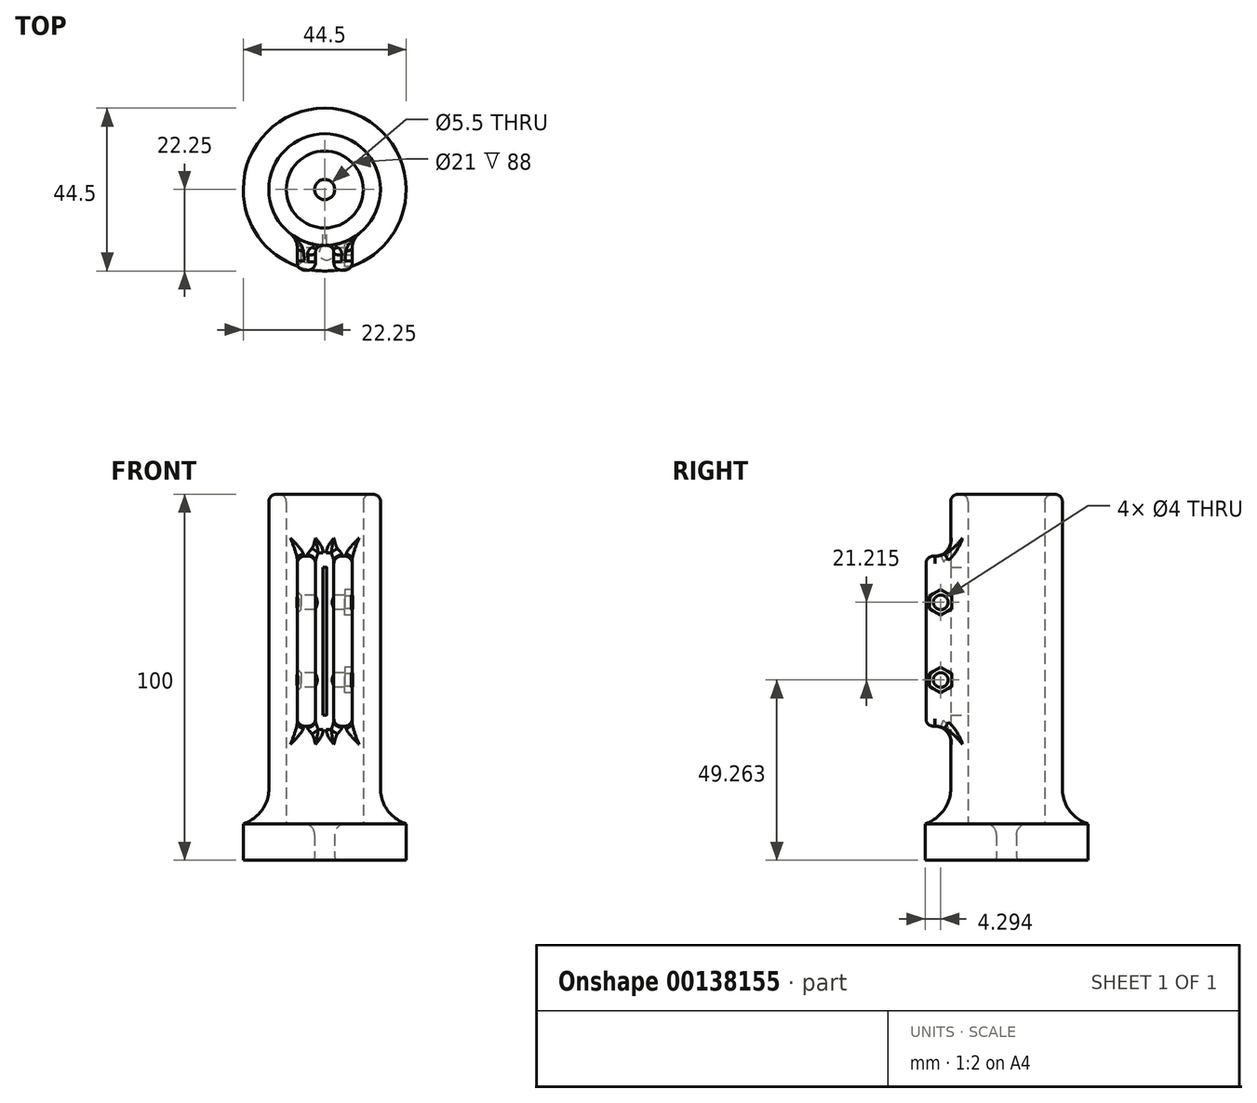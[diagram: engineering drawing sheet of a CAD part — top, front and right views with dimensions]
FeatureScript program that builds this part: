
annotation { "Feature Type Name" : "Feature", "Feature Type Description" : "" }
export const myFeature = defineFeature(function(context is Context, id is Id, definition is map)
    precondition{}
    {
        {
            var Q0;
            Q0=qCreatedBy(makeId("Top.planeOp"),FACE);
            var sketch = newSketch(context, id + "F0", { "sketchPlane" : qUnion([Q0])});
            skCircle(sketch, "E0", {"center": v(0, 0) * mm, "radius": 22.25 * mm});
            skCircle(sketch, "E1", {"center": v(0, 0) * mm, "radius": 2.75 * mm});
            skCircle(sketch, "E2", {"center": v(0, 0) * mm, "radius": 10.5 * mm});
            skCircle(sketch, "E3", {"center": v(0, 0) * mm, "radius": 15.25 * mm});
            skSolve(sketch);
        }
        {
            var Q0;
            Q0=makeQuery(id+"F0.imprint","IMPRINT",FACE,{"disambiguationData":[TD([[makeQuery(id+"F0.imprint","IMPRINT",EDGE,{"derivedFrom":sQuery(id+"F0.wireOp",EDGE,"E0")}),1.0]])]});
            var Q1;
            Q1=makeQuery(id+"F0.imprint","IMPRINT",FACE,{"disambiguationData":[TD([[makeQuery(id+"F0.imprint","IMPRINT",EDGE,{"derivedFrom":sQuery(id+"F0.wireOp",EDGE,"E2")}),-1.0]])]});
            var Q2;
            Q2=makeQuery(id+"F0.imprint","IMPRINT",FACE,{"disambiguationData":[TD([[makeQuery(id+"F0.imprint","IMPRINT",EDGE,{"derivedFrom":sQuery(id+"F0.wireOp",EDGE,"E1")}),-1.0]])]});
            extrude(context, id + "F1", {"entities" : qUnion([Q0, Q1, Q2]), "depth" : 10 * mm});
        }
        {
            var Q0;
            Q0=makeQuery(id+"F0.imprint","IMPRINT",FACE,{"disambiguationData":[TD([[makeQuery(id+"F0.imprint","IMPRINT",EDGE,{"derivedFrom":sQuery(id+"F0.wireOp",EDGE,"E2")}),-1.0]])]});
            extrude(context, id + "F2", {"entities" : qUnion([Q0]), "operationType" : NewBodyOperationType.ADD, "depth" : 100 * mm});
        }
        {
            var Q0;
            Q0=makeQuery(id+"F1.opExtrude","CAP_EDGE",EDGE,{"disambiguationData":[OSD([sQuery(id+"F0.wireOp",EDGE,"E1")])],"isStart":false});
            fillet(context, id + "F3", {"entities" : qUnion([Q0]), "radius" : 3 * mm, "tangentPropagation" : true, "allowEdgeOverflow" : false});
        }
        {
            var Q0;
            Q0=makeQuery(id+"F1.opExtrude","CAP_EDGE",EDGE,{"disambiguationData":[OSD([sQuery(id+"F0.wireOp",EDGE,"E1")])],"isStart":true});
            fillet(context, id + "F4", {"entities" : qUnion([Q0]), "radius" : 1 * mm, "tangentPropagation" : true, "allowEdgeOverflow" : false});
        }
        {
            var Q0;
            Q0=makeQuery(id+"F2.boolean.opBoolean","INTERSECT",EDGE,{"derivedFrom":[makeQuery(id+"F1.opExtrude","CAP_FACE",FACE,{"disambiguationData":[OSD([sQuery(id+"F0.wireOp",EDGE,"E0"),sQuery(id+"F0.wireOp",EDGE,"E1")])],"isStart":false}),makeQuery(id+"F2.opExtrude","SWEPT_FACE",FACE,{"disambiguationData":[OSD([sQuery(id+"F0.wireOp",EDGE,"E3")])]})]});
            fillet(context, id + "F5", {"entities" : qUnion([Q0]), "radius" : 10 * mm, "tangentPropagation" : true, "allowEdgeOverflow" : false});
        }
        {
            var Q0;
            Q0=makeQuery(id+"F2.opExtrude","CAP_EDGE",EDGE,{"disambiguationData":[OSD([sQuery(id+"F0.wireOp",EDGE,"E3")])],"isStart":false});
            fillet(context, id + "F6", {"entities" : qUnion([Q0]), "radius" : 2 * mm, "tangentPropagation" : true, "allowEdgeOverflow" : false});
        }
        {
            var Q0;
            Q0=makeQuery(id+"F2.opExtrude","CAP_EDGE",EDGE,{"disambiguationData":[OSD([sQuery(id+"F0.wireOp",EDGE,"E2")])],"isStart":false});
            fillet(context, id + "F7", {"entities" : qUnion([Q0]), "radius" : 2 * mm, "tangentPropagation" : true, "allowEdgeOverflow" : false});
        }
        {
            var Q0;
            Q0=qCreatedBy(makeId("Front.planeOp"),FACE);
            var sketch = newSketch(context, id + "F8", { "sketchPlane" : qUnion([Q0])});
            skPoint(sketch, "E4", {"position": v(0, 100.09) * mm});
            skPoint(sketch, "E5", {"position": v(0, 19.65) * mm});
            skPoint(sketch, "E6", {"position": v(0, 39.65) * mm});
            skPoint(sketch, "E7", {"position": v(0, 80.09) * mm});
            skPoint(sketch, "E8", {"position": v(0.5, 80.09) * mm});
            skPoint(sketch, "E9", {"position": v(-0.5, 80.09) * mm});
            skPoint(sketch, "E10", {"position": v(0.5, 39.65) * mm});
            skPoint(sketch, "E11", {"position": v(-0.5, 39.65) * mm});
            skLineSegment(sketch, "E12", {"start": v(-0.5, 80.09) * mm, "end": v(0.5, 80.09) * mm});
            skLineSegment(sketch, "E13", {"start": v(0.5, 39.65) * mm, "end": v(-0.5, 39.65) * mm});
            skLineSegment(sketch, "E14", {"start": v(-0.5, 39.65) * mm, "end": v(-0.5, 80.09) * mm});
            skLineSegment(sketch, "E15", {"start": v(0.5, 39.65) * mm, "end": v(0.5, 80.09) * mm});
            skPoint(sketch, "E16", {"position": v(-2.5, 83.09) * mm});
            skPoint(sketch, "E17", {"position": v(-2.5, 36.65) * mm});
            skPoint(sketch, "E18", {"position": v(-7.5, 83.09) * mm});
            skPoint(sketch, "E19", {"position": v(-7.5, 36.65) * mm});
            skLineSegment(sketch, "E20", {"start": v(-2.5, 36.65) * mm, "end": v(-7.5, 36.65) * mm});
            skLineSegment(sketch, "E21", {"start": v(-2.5, 83.09) * mm, "end": v(-2.5, 36.65) * mm});
            skLineSegment(sketch, "E22", {"start": v(-7.5, 83.09) * mm, "end": v(-7.5, 36.65) * mm});
            skLineSegment(sketch, "E23", {"start": v(-7.5, 83.09) * mm, "end": v(-2.5, 83.09) * mm});
            skPoint(sketch, "E24", {"position": v(-2.5, 80.09) * mm});
            skPoint(sketch, "E25", {"position": v(-2.5, 39.65) * mm});
            skPoint(sketch, "E26", {"position": v(2.5, 80.09) * mm});
            skPoint(sketch, "E27", {"position": v(2.5, 39.65) * mm});
            skPoint(sketch, "E28", {"position": v(2.5, 83.09) * mm});
            skPoint(sketch, "E29", {"position": v(2.5, 36.65) * mm});
            skLineSegment(sketch, "E30", {"start": v(2.5, 83.09) * mm, "end": v(2.5, 39.65) * mm});
            skLineSegment(sketch, "E31", {"start": v(2.5, 83.09) * mm, "end": v(7.5, 83.09) * mm});
            skLineSegment(sketch, "E32", {"start": v(2.5, 83.09) * mm, "end": v(2.5, 36.65) * mm});
            skLineSegment(sketch, "E33", {"start": v(7.5, 36.65) * mm, "end": v(2.5, 36.65) * mm});
            skLineSegment(sketch, "E34", {"start": v(7.5, 83.09) * mm, "end": v(7.5, 36.65) * mm});
            skSolve(sketch);
        }
        {
            var Q0;
            Q0=makeQuery(id+"F8.imprint","IMPRINT",FACE,{"disambiguationData":[TD([[makeQuery(id+"F8.imprint","IMPRINT",EDGE,{"derivedFrom":sQuery(id+"F8.wireOp",EDGE,"E12")}),-1.0]])]});
            extrude(context, id + "F9", {"entities" : qUnion([Q0]), "operationType" : NewBodyOperationType.REMOVE, "depth" : 50 * mm});
        }
        {
            var Q0;
            Q0=makeQuery(id+"F8.imprint","IMPRINT",FACE,{"disambiguationData":[TD([[makeQuery(id+"F8.imprint","IMPRINT",EDGE,{"derivedFrom":sQuery(id+"F8.wireOp",EDGE,"E20")}),-1.0]])]});
            var Q1;
            {var subQ0=sQuery(id+"F8.wireOp",EDGE,"E31");Q1=makeQuery(id+"F8.imprint","IMPRINT",FACE,{"disambiguationData":[TD([[makeQuery(id+"F8.imprint","IMPRINT",EDGE,{"derivedFrom":subQ0}),-1.0]])]});}
            extrude(context, id + "F10", {"entities" : qUnion([Q0, Q1]), "operationType" : NewBodyOperationType.ADD, "depth" : 22 * mm, "hasSecondDirection" : true, "secondDirectionOppositeDirection" : false, "secondDirectionDepth" : 10.1 * mm});
        }
        {
            var Q0;
            {var subQ0=sQuery(id+"F0.wireOp",EDGE,"E1");Q0=makeQuery(id+"F2.boolean.opBoolean","SPLIT",FACE,{"disambiguationData":[TD([makeQuery(id+"F1.opExtrude","SWEPT_FACE",FACE,{"disambiguationData":[OSD([subQ0])]})])],"derivedFrom":makeQuery(id+"F1.opExtrude","CAP_FACE",FACE,{"disambiguationData":[OSD([sQuery(id+"F0.wireOp",EDGE,"E0"),subQ0])],"isStart":false})});}
            var Q1;
            Q1=makeQuery(id+"F0.imprint","IMPRINT",FACE,{"disambiguationData":[TD([[makeQuery(id+"F0.imprint","IMPRINT",EDGE,{"derivedFrom":sQuery(id+"F0.wireOp",EDGE,"E1")}),1.0]])]});
            extrude(context, id + "F11", {"entities" : qUnion([Q0, Q1]), "operationType" : NewBodyOperationType.REMOVE, "depth" : 150 * mm});
        }
        {
            var Q0;
            Q0=makeQuery(id+"F10.boolean.opBoolean","INTERSECT",EDGE,{"derivedFrom":[makeQuery(id+"F2.opExtrude","SWEPT_FACE",FACE,{"disambiguationData":[OSD([sQuery(id+"F0.wireOp",EDGE,"E3")])]}),makeQuery(id+"F10.opExtrude","SWEPT_FACE",FACE,{"disambiguationData":[OSD([sQuery(id+"F8.wireOp",EDGE,"E23")])]})]});
            var Q1;
            Q1=makeQuery(id+"F10.boolean.opBoolean","INTERSECT",EDGE,{"derivedFrom":[makeQuery(id+"F2.opExtrude","SWEPT_FACE",FACE,{"disambiguationData":[OSD([sQuery(id+"F0.wireOp",EDGE,"E3")])]}),makeQuery(id+"F10.opExtrude","SWEPT_FACE",FACE,{"disambiguationData":[OSD([sQuery(id+"F8.wireOp",EDGE,"E31")])]})]});
            var Q2;
            Q2=makeQuery(id+"F10.boolean.opBoolean","INTERSECT",EDGE,{"derivedFrom":[makeQuery(id+"F2.opExtrude","SWEPT_FACE",FACE,{"disambiguationData":[OSD([sQuery(id+"F0.wireOp",EDGE,"E3")])]}),makeQuery(id+"F10.opExtrude","SWEPT_FACE",FACE,{"disambiguationData":[OSD([sQuery(id+"F8.wireOp",EDGE,"E33")])]})]});
            var Q3;
            Q3=makeQuery(id+"F10.boolean.opBoolean","INTERSECT",EDGE,{"derivedFrom":[makeQuery(id+"F2.opExtrude","SWEPT_FACE",FACE,{"disambiguationData":[OSD([sQuery(id+"F0.wireOp",EDGE,"E3")])]}),makeQuery(id+"F10.opExtrude","SWEPT_FACE",FACE,{"disambiguationData":[OSD([sQuery(id+"F8.wireOp",EDGE,"E20")])]})]});
            fillet(context, id + "F12", {"entities" : qUnion([Q0, Q1, Q2, Q3]), "radius" : 5 * mm, "tangentPropagation" : true, "allowEdgeOverflow" : false});
        }
        {
            var Q0;
            Q0=makeQuery(id+"F10.boolean.opBoolean","INTERSECT",EDGE,{"derivedFrom":[makeQuery(id+"F2.opExtrude","SWEPT_FACE",FACE,{"disambiguationData":[OSD([sQuery(id+"F0.wireOp",EDGE,"E3")])]}),makeQuery(id+"F10.opExtrude","SWEPT_FACE",FACE,{"disambiguationData":[OSD([sQuery(id+"F8.wireOp",EDGE,"E21")])]})]});
            var Q1;
            Q1=makeQuery(id+"F10.boolean.opBoolean","INTERSECT",EDGE,{"derivedFrom":[makeQuery(id+"F2.opExtrude","SWEPT_FACE",FACE,{"disambiguationData":[OSD([sQuery(id+"F0.wireOp",EDGE,"E3")])]}),makeQuery(id+"F10.opExtrude","SWEPT_FACE",FACE,{"disambiguationData":[OSD([sQuery(id+"F8.wireOp",EDGE,"E32")])]})]});
            fillet(context, id + "F13", {"entities" : qUnion([Q0, Q1]), "radius" : 2 * mm, "tangentPropagation" : true, "allowEdgeOverflow" : false});
        }
        {
            var Q0;
            Q0=makeQuery(id+"F10.boolean.opBoolean","INTERSECT",EDGE,{"derivedFrom":[makeQuery(id+"F2.opExtrude","SWEPT_FACE",FACE,{"disambiguationData":[OSD([sQuery(id+"F0.wireOp",EDGE,"E3")])]}),makeQuery(id+"F10.opExtrude","SWEPT_FACE",FACE,{"disambiguationData":[OSD([sQuery(id+"F8.wireOp",EDGE,"E22")])]})]});
            var Q1;
            Q1=makeQuery(id+"F10.boolean.opBoolean","INTERSECT",EDGE,{"derivedFrom":[makeQuery(id+"F2.opExtrude","SWEPT_FACE",FACE,{"disambiguationData":[OSD([sQuery(id+"F0.wireOp",EDGE,"E3")])]}),makeQuery(id+"F10.opExtrude","SWEPT_FACE",FACE,{"disambiguationData":[OSD([sQuery(id+"F8.wireOp",EDGE,"E34")])]})]});
            fillet(context, id + "F14", {"entities" : qUnion([Q0, Q1]), "radius" : 5 * mm, "tangentPropagation" : true, "allowEdgeOverflow" : false});
        }
        {
            var Q0;
            Q0=makeQuery(id+"F10.opExtrude","CAP_EDGE",EDGE,{"disambiguationData":[OSD([sQuery(id+"F8.wireOp",EDGE,"E31")])],"isStart":false});
            var Q1;
            Q1=makeQuery(id+"F10.opExtrude","CAP_EDGE",EDGE,{"disambiguationData":[OSD([sQuery(id+"F8.wireOp",EDGE,"E34")])],"isStart":false});
            var Q2;
            Q2=makeQuery(id+"F10.opExtrude","CAP_EDGE",EDGE,{"disambiguationData":[OSD([sQuery(id+"F8.wireOp",EDGE,"E33")])],"isStart":false});
            var Q3;
            Q3=makeQuery(id+"F10.opExtrude","CAP_EDGE",EDGE,{"disambiguationData":[OSD([sQuery(id+"F8.wireOp",EDGE,"E20")])],"isStart":false});
            var Q4;
            Q4=makeQuery(id+"F10.opExtrude","CAP_EDGE",EDGE,{"disambiguationData":[OSD([sQuery(id+"F8.wireOp",EDGE,"E22")])],"isStart":false});
            var Q5;
            Q5=makeQuery(id+"F10.opExtrude","CAP_EDGE",EDGE,{"disambiguationData":[OSD([sQuery(id+"F8.wireOp",EDGE,"E23")])],"isStart":false});
            fillet(context, id + "F15", {"entities" : qUnion([Q0, Q1, Q2, Q3, Q4, Q5]), "radius" : 2 * mm, "tangentPropagation" : true, "allowEdgeOverflow" : false});
        }
        {
            var Q0;
            {var subQ0=sQuery(id+"F0.wireOp",EDGE,"E3");Q0=makeQuery(id+"F14.opFillet","BLEND_EDGE",EDGE,{"blendedFrom":[makeQuery(id+"F10.boolean.opBoolean","INTERSECT",EDGE,{"derivedFrom":[makeQuery(id+"F2.opExtrude","SWEPT_FACE",FACE,{"disambiguationData":[OSD([subQ0])]}),makeQuery(id+"F10.opExtrude","SWEPT_FACE",FACE,{"disambiguationData":[OSD([sQuery(id+"F8.wireOp",EDGE,"E34")])]})]}),makeQuery(id+"F12.opFillet","BLEND_FACE",FACE,{"disambiguationData":[OSD([subQ0,sQuery(id+"F8.wireOp",EDGE,"E31")])]})],"blendedInto":[makeQuery(id+"F12.opFillet","BLEND_FACE",FACE,{"disambiguationData":[OSD([subQ0,sQuery(id+"F8.wireOp",EDGE,"E31")])]})]});}
            var Q1;
            {var subQ0=makeQuery(id+"F2.opExtrude","SWEPT_FACE",FACE,{"disambiguationData":[OSD([sQuery(id+"F0.wireOp",EDGE,"E3")])]});var subQ1=sQuery(id+"F8.wireOp",EDGE,"E31");var subQ2=makeQuery(id+"F10.opExtrude","SWEPT_FACE",FACE,{"disambiguationData":[OSD([subQ1])]});var subQ3=sQuery(id+"F8.wireOp",EDGE,"E34");Q1=makeQuery(id+"F12.opFillet","BLEND_EDGE",EDGE,{"blendedFrom":[makeQuery(id+"F10.boolean.opBoolean","INTERSECT",EDGE,{"derivedFrom":[subQ0,subQ2]}),makeQuery(id+"F10.boolean.opBoolean","SPLIT",FACE,{"disambiguationData":[TD([subQ0])],"derivedFrom":makeQuery(id+"F10.opExtrude","SWEPT_FACE",FACE,{"disambiguationData":[OSD([subQ3])]})})],"blendedInto":[makeQuery(id+"F10.boolean.opBoolean","SPLIT",FACE,{"disambiguationData":[TD([subQ0])],"derivedFrom":makeQuery(id+"F10.opExtrude","SWEPT_FACE",FACE,{"disambiguationData":[OSD([subQ3])]})})]});}
            var Q2;
            {var subQ0=makeQuery(id+"F2.opExtrude","SWEPT_FACE",FACE,{"disambiguationData":[OSD([sQuery(id+"F0.wireOp",EDGE,"E3")])]});var subQ1=sQuery(id+"F8.wireOp",EDGE,"E23");var subQ2=sQuery(id+"F8.wireOp",EDGE,"E22");var subQ4=makeQuery(id+"F10.opExtrude","SWEPT_FACE",FACE,{"disambiguationData":[OSD([subQ1])]});Q2=makeQuery(id+"F12.opFillet","BLEND_EDGE",EDGE,{"blendedFrom":[makeQuery(id+"F10.boolean.opBoolean","INTERSECT",EDGE,{"derivedFrom":[subQ0,subQ4]}),makeQuery(id+"F10.boolean.opBoolean","SPLIT",FACE,{"disambiguationData":[TD([subQ0])],"derivedFrom":makeQuery(id+"F10.opExtrude","SWEPT_FACE",FACE,{"disambiguationData":[OSD([subQ2])]})})],"blendedInto":[makeQuery(id+"F10.boolean.opBoolean","SPLIT",FACE,{"disambiguationData":[TD([subQ0])],"derivedFrom":makeQuery(id+"F10.opExtrude","SWEPT_FACE",FACE,{"disambiguationData":[OSD([subQ2])]})})]});}
            var Q3;
            {var subQ0=sQuery(id+"F0.wireOp",EDGE,"E3");Q3=makeQuery(id+"F14.opFillet","BLEND_EDGE",EDGE,{"blendedFrom":[makeQuery(id+"F10.boolean.opBoolean","INTERSECT",EDGE,{"derivedFrom":[makeQuery(id+"F2.opExtrude","SWEPT_FACE",FACE,{"disambiguationData":[OSD([subQ0])]}),makeQuery(id+"F10.opExtrude","SWEPT_FACE",FACE,{"disambiguationData":[OSD([sQuery(id+"F8.wireOp",EDGE,"E22")])]})]}),makeQuery(id+"F12.opFillet","BLEND_FACE",FACE,{"disambiguationData":[OSD([subQ0,sQuery(id+"F8.wireOp",EDGE,"E23")])]})],"blendedInto":[makeQuery(id+"F12.opFillet","BLEND_FACE",FACE,{"disambiguationData":[OSD([subQ0,sQuery(id+"F8.wireOp",EDGE,"E23")])]})]});}
            var Q4;
            {var subQ0=sQuery(id+"F0.wireOp",EDGE,"E3");Q4=makeQuery(id+"F13.opFillet","BLEND_EDGE",EDGE,{"blendedFrom":[makeQuery(id+"F10.boolean.opBoolean","INTERSECT",EDGE,{"derivedFrom":[makeQuery(id+"F2.opExtrude","SWEPT_FACE",FACE,{"disambiguationData":[OSD([subQ0])]}),makeQuery(id+"F10.opExtrude","SWEPT_FACE",FACE,{"disambiguationData":[OSD([sQuery(id+"F8.wireOp",EDGE,"E21")])]})]}),makeQuery(id+"F12.opFillet","BLEND_FACE",FACE,{"disambiguationData":[OSD([subQ0,sQuery(id+"F8.wireOp",EDGE,"E23")])]})],"blendedInto":[makeQuery(id+"F12.opFillet","BLEND_FACE",FACE,{"disambiguationData":[OSD([subQ0,sQuery(id+"F8.wireOp",EDGE,"E23")])]})]});}
            var Q5;
            {var subQ0=makeQuery(id+"F2.opExtrude","SWEPT_FACE",FACE,{"disambiguationData":[OSD([sQuery(id+"F0.wireOp",EDGE,"E3")])]});var subQ1=sQuery(id+"F8.wireOp",EDGE,"E23");var subQ2=sQuery(id+"F8.wireOp",EDGE,"E21");var subQ4=makeQuery(id+"F10.opExtrude","SWEPT_FACE",FACE,{"disambiguationData":[OSD([subQ1])]});Q5=makeQuery(id+"F12.opFillet","BLEND_EDGE",EDGE,{"blendedFrom":[makeQuery(id+"F10.boolean.opBoolean","INTERSECT",EDGE,{"derivedFrom":[subQ0,subQ4]}),makeQuery(id+"F10.boolean.opBoolean","SPLIT",FACE,{"disambiguationData":[TD([subQ0])],"derivedFrom":makeQuery(id+"F10.opExtrude","SWEPT_FACE",FACE,{"disambiguationData":[OSD([subQ2])]})})],"blendedInto":[makeQuery(id+"F10.boolean.opBoolean","SPLIT",FACE,{"disambiguationData":[TD([subQ0])],"derivedFrom":makeQuery(id+"F10.opExtrude","SWEPT_FACE",FACE,{"disambiguationData":[OSD([subQ2])]})})]});}
            var Q6;
            {var subQ0=sQuery(id+"F0.wireOp",EDGE,"E3");Q6=makeQuery(id+"F13.opFillet","BLEND_EDGE",EDGE,{"blendedFrom":[makeQuery(id+"F10.boolean.opBoolean","INTERSECT",EDGE,{"derivedFrom":[makeQuery(id+"F2.opExtrude","SWEPT_FACE",FACE,{"disambiguationData":[OSD([subQ0])]}),makeQuery(id+"F10.opExtrude","SWEPT_FACE",FACE,{"disambiguationData":[OSD([sQuery(id+"F8.wireOp",EDGE,"E32")])]})]}),makeQuery(id+"F12.opFillet","BLEND_FACE",FACE,{"disambiguationData":[OSD([subQ0,sQuery(id+"F8.wireOp",EDGE,"E31")])]})],"blendedInto":[makeQuery(id+"F12.opFillet","BLEND_FACE",FACE,{"disambiguationData":[OSD([subQ0,sQuery(id+"F8.wireOp",EDGE,"E31")])]})]});}
            var Q7;
            {var subQ0=makeQuery(id+"F2.opExtrude","SWEPT_FACE",FACE,{"disambiguationData":[OSD([sQuery(id+"F0.wireOp",EDGE,"E3")])]});var subQ1=sQuery(id+"F8.wireOp",EDGE,"E31");var subQ2=makeQuery(id+"F10.opExtrude","SWEPT_FACE",FACE,{"disambiguationData":[OSD([subQ1])]});var subQ4=sQuery(id+"F8.wireOp",EDGE,"E32");Q7=makeQuery(id+"F12.opFillet","BLEND_EDGE",EDGE,{"blendedFrom":[makeQuery(id+"F10.boolean.opBoolean","INTERSECT",EDGE,{"derivedFrom":[subQ0,subQ2]}),makeQuery(id+"F10.boolean.opBoolean","SPLIT",FACE,{"disambiguationData":[TD([subQ0])],"derivedFrom":makeQuery(id+"F10.opExtrude","SWEPT_FACE",FACE,{"disambiguationData":[OSD([subQ4])]})})],"blendedInto":[makeQuery(id+"F10.boolean.opBoolean","SPLIT",FACE,{"disambiguationData":[TD([subQ0])],"derivedFrom":makeQuery(id+"F10.opExtrude","SWEPT_FACE",FACE,{"disambiguationData":[OSD([subQ4])]})})]});}
            var Q8;
            {var subQ0=sQuery(id+"F8.wireOp",EDGE,"E31");var subQ1=sQuery(id+"F8.wireOp",EDGE,"E34");Q8=makeQuery(id+"F10.boolean.opBoolean","SPLIT",EDGE,{"disambiguationData":[TD([makeQuery(id+"F2.opExtrude","SWEPT_FACE",FACE,{"disambiguationData":[OSD([sQuery(id+"F0.wireOp",EDGE,"E3")])]})])],"derivedFrom":makeQuery(id+"F10.opExtrude","SWEPT_EDGE",EDGE,{"disambiguationData":[OSD([subQ0,subQ1])]})});}
            var Q9;
            Q9=makeQuery(id+"F15.opFillet","BLEND_EDGE",EDGE,{"blendedFrom":[makeQuery(id+"F10.opExtrude","CAP_EDGE",EDGE,{"disambiguationData":[OSD([sQuery(id+"F8.wireOp",EDGE,"E31")])],"isStart":false}),makeQuery(id+"F10.opExtrude","CAP_EDGE",EDGE,{"disambiguationData":[OSD([sQuery(id+"F8.wireOp",EDGE,"E34")])],"isStart":false})],"blendedInto":[]});
            var Q10;
            {var subQ0=sQuery(id+"F8.wireOp",EDGE,"E31");var subQ2=sQuery(id+"F8.wireOp",EDGE,"E32");Q10=makeQuery(id+"F15.opFillet","BLEND_EDGE",EDGE,{"blendedFrom":[makeQuery(id+"F10.opExtrude","CAP_EDGE",EDGE,{"disambiguationData":[OSD([subQ0])],"isStart":false}),makeQuery(id+"F10.boolean.opBoolean","SPLIT",FACE,{"disambiguationData":[TD([makeQuery(id+"F2.opExtrude","SWEPT_FACE",FACE,{"disambiguationData":[OSD([sQuery(id+"F0.wireOp",EDGE,"E3")])]})])],"derivedFrom":makeQuery(id+"F10.opExtrude","SWEPT_FACE",FACE,{"disambiguationData":[OSD([subQ2])]})})],"blendedInto":[makeQuery(id+"F10.boolean.opBoolean","SPLIT",FACE,{"disambiguationData":[TD([makeQuery(id+"F2.opExtrude","SWEPT_FACE",FACE,{"disambiguationData":[OSD([sQuery(id+"F0.wireOp",EDGE,"E3")])]})])],"derivedFrom":makeQuery(id+"F10.opExtrude","SWEPT_FACE",FACE,{"disambiguationData":[OSD([subQ2])]})})]});}
            var Q11;
            {var subQ0=sQuery(id+"F8.wireOp",EDGE,"E23");var subQ1=sQuery(id+"F8.wireOp",EDGE,"E21");Q11=makeQuery(id+"F15.opFillet","BLEND_EDGE",EDGE,{"blendedFrom":[makeQuery(id+"F10.opExtrude","CAP_EDGE",EDGE,{"disambiguationData":[OSD([subQ0])],"isStart":false}),makeQuery(id+"F10.boolean.opBoolean","SPLIT",FACE,{"disambiguationData":[TD([makeQuery(id+"F2.opExtrude","SWEPT_FACE",FACE,{"disambiguationData":[OSD([sQuery(id+"F0.wireOp",EDGE,"E3")])]})])],"derivedFrom":makeQuery(id+"F10.opExtrude","SWEPT_FACE",FACE,{"disambiguationData":[OSD([subQ1])]})})],"blendedInto":[makeQuery(id+"F10.boolean.opBoolean","SPLIT",FACE,{"disambiguationData":[TD([makeQuery(id+"F2.opExtrude","SWEPT_FACE",FACE,{"disambiguationData":[OSD([sQuery(id+"F0.wireOp",EDGE,"E3")])]})])],"derivedFrom":makeQuery(id+"F10.opExtrude","SWEPT_FACE",FACE,{"disambiguationData":[OSD([subQ1])]})})]});}
            var Q12;
            {var subQ0=sQuery(id+"F8.wireOp",EDGE,"E23");var subQ1=sQuery(id+"F8.wireOp",EDGE,"E22");Q12=makeQuery(id+"F10.boolean.opBoolean","SPLIT",EDGE,{"disambiguationData":[TD([makeQuery(id+"F2.opExtrude","SWEPT_FACE",FACE,{"disambiguationData":[OSD([sQuery(id+"F0.wireOp",EDGE,"E3")])]})])],"derivedFrom":makeQuery(id+"F10.opExtrude","SWEPT_EDGE",EDGE,{"disambiguationData":[OSD([subQ1,subQ0])]})});}
            var Q13;
            Q13=makeQuery(id+"F15.opFillet","BLEND_EDGE",EDGE,{"blendedFrom":[makeQuery(id+"F10.opExtrude","CAP_EDGE",EDGE,{"disambiguationData":[OSD([sQuery(id+"F8.wireOp",EDGE,"E22")])],"isStart":false}),makeQuery(id+"F10.opExtrude","CAP_EDGE",EDGE,{"disambiguationData":[OSD([sQuery(id+"F8.wireOp",EDGE,"E23")])],"isStart":false})],"blendedInto":[]});
            var Q14;
            {var subQ0=sQuery(id+"F0.wireOp",EDGE,"E3");Q14=makeQuery(id+"F14.opFillet","BLEND_EDGE",EDGE,{"blendedFrom":[makeQuery(id+"F10.boolean.opBoolean","INTERSECT",EDGE,{"derivedFrom":[makeQuery(id+"F2.opExtrude","SWEPT_FACE",FACE,{"disambiguationData":[OSD([subQ0])]}),makeQuery(id+"F10.opExtrude","SWEPT_FACE",FACE,{"disambiguationData":[OSD([sQuery(id+"F8.wireOp",EDGE,"E34")])]})]}),makeQuery(id+"F12.opFillet","BLEND_FACE",FACE,{"disambiguationData":[OSD([subQ0,sQuery(id+"F8.wireOp",EDGE,"E33")])]})],"blendedInto":[makeQuery(id+"F12.opFillet","BLEND_FACE",FACE,{"disambiguationData":[OSD([subQ0,sQuery(id+"F8.wireOp",EDGE,"E33")])]})]});}
            var Q15;
            {var subQ0=makeQuery(id+"F2.opExtrude","SWEPT_FACE",FACE,{"disambiguationData":[OSD([sQuery(id+"F0.wireOp",EDGE,"E3")])]});var subQ2=sQuery(id+"F8.wireOp",EDGE,"E34");var subQ3=sQuery(id+"F8.wireOp",EDGE,"E33");var subQ4=makeQuery(id+"F10.opExtrude","SWEPT_FACE",FACE,{"disambiguationData":[OSD([subQ3])]});Q15=makeQuery(id+"F12.opFillet","BLEND_EDGE",EDGE,{"blendedFrom":[makeQuery(id+"F10.boolean.opBoolean","INTERSECT",EDGE,{"derivedFrom":[subQ0,subQ4]}),makeQuery(id+"F10.boolean.opBoolean","SPLIT",FACE,{"disambiguationData":[TD([subQ0])],"derivedFrom":makeQuery(id+"F10.opExtrude","SWEPT_FACE",FACE,{"disambiguationData":[OSD([subQ2])]})})],"blendedInto":[makeQuery(id+"F10.boolean.opBoolean","SPLIT",FACE,{"disambiguationData":[TD([subQ0])],"derivedFrom":makeQuery(id+"F10.opExtrude","SWEPT_FACE",FACE,{"disambiguationData":[OSD([subQ2])]})})]});}
            var Q16;
            {var subQ0=sQuery(id+"F8.wireOp",EDGE,"E34");var subQ1=sQuery(id+"F8.wireOp",EDGE,"E33");Q16=makeQuery(id+"F10.boolean.opBoolean","SPLIT",EDGE,{"disambiguationData":[TD([makeQuery(id+"F2.opExtrude","SWEPT_FACE",FACE,{"disambiguationData":[OSD([sQuery(id+"F0.wireOp",EDGE,"E3")])]})])],"derivedFrom":makeQuery(id+"F10.opExtrude","SWEPT_EDGE",EDGE,{"disambiguationData":[OSD([subQ1,subQ0])]})});}
            var Q17;
            Q17=makeQuery(id+"F15.opFillet","BLEND_EDGE",EDGE,{"blendedFrom":[makeQuery(id+"F10.opExtrude","CAP_EDGE",EDGE,{"disambiguationData":[OSD([sQuery(id+"F8.wireOp",EDGE,"E33")])],"isStart":false}),makeQuery(id+"F10.opExtrude","CAP_EDGE",EDGE,{"disambiguationData":[OSD([sQuery(id+"F8.wireOp",EDGE,"E34")])],"isStart":false})],"blendedInto":[]});
            var Q18;
            {var subQ1=sQuery(id+"F8.wireOp",EDGE,"E33");var subQ2=sQuery(id+"F8.wireOp",EDGE,"E32");Q18=makeQuery(id+"F15.opFillet","BLEND_EDGE",EDGE,{"blendedFrom":[makeQuery(id+"F10.opExtrude","CAP_EDGE",EDGE,{"disambiguationData":[OSD([subQ1])],"isStart":false}),makeQuery(id+"F10.boolean.opBoolean","SPLIT",FACE,{"disambiguationData":[TD([makeQuery(id+"F2.opExtrude","SWEPT_FACE",FACE,{"disambiguationData":[OSD([sQuery(id+"F0.wireOp",EDGE,"E3")])]})])],"derivedFrom":makeQuery(id+"F10.opExtrude","SWEPT_FACE",FACE,{"disambiguationData":[OSD([subQ2])]})})],"blendedInto":[makeQuery(id+"F10.boolean.opBoolean","SPLIT",FACE,{"disambiguationData":[TD([makeQuery(id+"F2.opExtrude","SWEPT_FACE",FACE,{"disambiguationData":[OSD([sQuery(id+"F0.wireOp",EDGE,"E3")])]})])],"derivedFrom":makeQuery(id+"F10.opExtrude","SWEPT_FACE",FACE,{"disambiguationData":[OSD([subQ2])]})})]});}
            var Q19;
            {var subQ0=makeQuery(id+"F2.opExtrude","SWEPT_FACE",FACE,{"disambiguationData":[OSD([sQuery(id+"F0.wireOp",EDGE,"E3")])]});var subQ2=sQuery(id+"F8.wireOp",EDGE,"E33");var subQ3=sQuery(id+"F8.wireOp",EDGE,"E32");var subQ4=makeQuery(id+"F10.opExtrude","SWEPT_FACE",FACE,{"disambiguationData":[OSD([subQ2])]});Q19=makeQuery(id+"F12.opFillet","BLEND_EDGE",EDGE,{"blendedFrom":[makeQuery(id+"F10.boolean.opBoolean","INTERSECT",EDGE,{"derivedFrom":[subQ0,subQ4]}),makeQuery(id+"F10.boolean.opBoolean","SPLIT",FACE,{"disambiguationData":[TD([subQ0])],"derivedFrom":makeQuery(id+"F10.opExtrude","SWEPT_FACE",FACE,{"disambiguationData":[OSD([subQ3])]})})],"blendedInto":[makeQuery(id+"F10.boolean.opBoolean","SPLIT",FACE,{"disambiguationData":[TD([subQ0])],"derivedFrom":makeQuery(id+"F10.opExtrude","SWEPT_FACE",FACE,{"disambiguationData":[OSD([subQ3])]})})]});}
            var Q20;
            {var subQ0=sQuery(id+"F0.wireOp",EDGE,"E3");Q20=makeQuery(id+"F13.opFillet","BLEND_EDGE",EDGE,{"blendedFrom":[makeQuery(id+"F10.boolean.opBoolean","INTERSECT",EDGE,{"derivedFrom":[makeQuery(id+"F2.opExtrude","SWEPT_FACE",FACE,{"disambiguationData":[OSD([subQ0])]}),makeQuery(id+"F10.opExtrude","SWEPT_FACE",FACE,{"disambiguationData":[OSD([sQuery(id+"F8.wireOp",EDGE,"E32")])]})]}),makeQuery(id+"F12.opFillet","BLEND_FACE",FACE,{"disambiguationData":[OSD([subQ0,sQuery(id+"F8.wireOp",EDGE,"E33")])]})],"blendedInto":[makeQuery(id+"F12.opFillet","BLEND_FACE",FACE,{"disambiguationData":[OSD([subQ0,sQuery(id+"F8.wireOp",EDGE,"E33")])]})]});}
            var Q21;
            {var subQ0=sQuery(id+"F0.wireOp",EDGE,"E3");Q21=makeQuery(id+"F13.opFillet","BLEND_EDGE",EDGE,{"blendedFrom":[makeQuery(id+"F10.boolean.opBoolean","INTERSECT",EDGE,{"derivedFrom":[makeQuery(id+"F2.opExtrude","SWEPT_FACE",FACE,{"disambiguationData":[OSD([subQ0])]}),makeQuery(id+"F10.opExtrude","SWEPT_FACE",FACE,{"disambiguationData":[OSD([sQuery(id+"F8.wireOp",EDGE,"E21")])]})]}),makeQuery(id+"F12.opFillet","BLEND_FACE",FACE,{"disambiguationData":[OSD([subQ0,sQuery(id+"F8.wireOp",EDGE,"E20")])]})],"blendedInto":[makeQuery(id+"F12.opFillet","BLEND_FACE",FACE,{"disambiguationData":[OSD([subQ0,sQuery(id+"F8.wireOp",EDGE,"E20")])]})]});}
            var Q22;
            {var subQ0=makeQuery(id+"F2.opExtrude","SWEPT_FACE",FACE,{"disambiguationData":[OSD([sQuery(id+"F0.wireOp",EDGE,"E3")])]});var subQ2=sQuery(id+"F8.wireOp",EDGE,"E21");var subQ3=sQuery(id+"F8.wireOp",EDGE,"E20");var subQ4=makeQuery(id+"F10.opExtrude","SWEPT_FACE",FACE,{"disambiguationData":[OSD([subQ3])]});Q22=makeQuery(id+"F12.opFillet","BLEND_EDGE",EDGE,{"blendedFrom":[makeQuery(id+"F10.boolean.opBoolean","INTERSECT",EDGE,{"derivedFrom":[subQ0,subQ4]}),makeQuery(id+"F10.boolean.opBoolean","SPLIT",FACE,{"disambiguationData":[TD([subQ0])],"derivedFrom":makeQuery(id+"F10.opExtrude","SWEPT_FACE",FACE,{"disambiguationData":[OSD([subQ2])]})})],"blendedInto":[makeQuery(id+"F10.boolean.opBoolean","SPLIT",FACE,{"disambiguationData":[TD([subQ0])],"derivedFrom":makeQuery(id+"F10.opExtrude","SWEPT_FACE",FACE,{"disambiguationData":[OSD([subQ2])]})})]});}
            var Q23;
            {var subQ1=sQuery(id+"F8.wireOp",EDGE,"E21");var subQ2=sQuery(id+"F8.wireOp",EDGE,"E20");Q23=makeQuery(id+"F15.opFillet","BLEND_EDGE",EDGE,{"blendedFrom":[makeQuery(id+"F10.opExtrude","CAP_EDGE",EDGE,{"disambiguationData":[OSD([subQ2])],"isStart":false}),makeQuery(id+"F10.boolean.opBoolean","SPLIT",FACE,{"disambiguationData":[TD([makeQuery(id+"F2.opExtrude","SWEPT_FACE",FACE,{"disambiguationData":[OSD([sQuery(id+"F0.wireOp",EDGE,"E3")])]})])],"derivedFrom":makeQuery(id+"F10.opExtrude","SWEPT_FACE",FACE,{"disambiguationData":[OSD([subQ1])]})})],"blendedInto":[makeQuery(id+"F10.boolean.opBoolean","SPLIT",FACE,{"disambiguationData":[TD([makeQuery(id+"F2.opExtrude","SWEPT_FACE",FACE,{"disambiguationData":[OSD([sQuery(id+"F0.wireOp",EDGE,"E3")])]})])],"derivedFrom":makeQuery(id+"F10.opExtrude","SWEPT_FACE",FACE,{"disambiguationData":[OSD([subQ1])]})})]});}
            var Q24;
            Q24=makeQuery(id+"F15.opFillet","BLEND_EDGE",EDGE,{"blendedFrom":[makeQuery(id+"F10.opExtrude","CAP_EDGE",EDGE,{"disambiguationData":[OSD([sQuery(id+"F8.wireOp",EDGE,"E20")])],"isStart":false}),makeQuery(id+"F10.opExtrude","CAP_EDGE",EDGE,{"disambiguationData":[OSD([sQuery(id+"F8.wireOp",EDGE,"E22")])],"isStart":false})],"blendedInto":[]});
            var Q25;
            {var subQ0=sQuery(id+"F8.wireOp",EDGE,"E22");var subQ1=sQuery(id+"F8.wireOp",EDGE,"E20");Q25=makeQuery(id+"F10.boolean.opBoolean","SPLIT",EDGE,{"disambiguationData":[TD([makeQuery(id+"F2.opExtrude","SWEPT_FACE",FACE,{"disambiguationData":[OSD([sQuery(id+"F0.wireOp",EDGE,"E3")])]})])],"derivedFrom":makeQuery(id+"F10.opExtrude","SWEPT_EDGE",EDGE,{"disambiguationData":[OSD([subQ1,subQ0])]})});}
            var Q26;
            {var subQ0=makeQuery(id+"F2.opExtrude","SWEPT_FACE",FACE,{"disambiguationData":[OSD([sQuery(id+"F0.wireOp",EDGE,"E3")])]});var subQ2=sQuery(id+"F8.wireOp",EDGE,"E22");var subQ3=sQuery(id+"F8.wireOp",EDGE,"E20");var subQ4=makeQuery(id+"F10.opExtrude","SWEPT_FACE",FACE,{"disambiguationData":[OSD([subQ3])]});Q26=makeQuery(id+"F12.opFillet","BLEND_EDGE",EDGE,{"blendedFrom":[makeQuery(id+"F10.boolean.opBoolean","INTERSECT",EDGE,{"derivedFrom":[subQ0,subQ4]}),makeQuery(id+"F10.boolean.opBoolean","SPLIT",FACE,{"disambiguationData":[TD([subQ0])],"derivedFrom":makeQuery(id+"F10.opExtrude","SWEPT_FACE",FACE,{"disambiguationData":[OSD([subQ2])]})})],"blendedInto":[makeQuery(id+"F10.boolean.opBoolean","SPLIT",FACE,{"disambiguationData":[TD([subQ0])],"derivedFrom":makeQuery(id+"F10.opExtrude","SWEPT_FACE",FACE,{"disambiguationData":[OSD([subQ2])]})})]});}
            var Q27;
            {var subQ0=sQuery(id+"F0.wireOp",EDGE,"E3");Q27=makeQuery(id+"F14.opFillet","BLEND_EDGE",EDGE,{"blendedFrom":[makeQuery(id+"F10.boolean.opBoolean","INTERSECT",EDGE,{"derivedFrom":[makeQuery(id+"F2.opExtrude","SWEPT_FACE",FACE,{"disambiguationData":[OSD([subQ0])]}),makeQuery(id+"F10.opExtrude","SWEPT_FACE",FACE,{"disambiguationData":[OSD([sQuery(id+"F8.wireOp",EDGE,"E22")])]})]}),makeQuery(id+"F12.opFillet","BLEND_FACE",FACE,{"disambiguationData":[OSD([subQ0,sQuery(id+"F8.wireOp",EDGE,"E20")])]})],"blendedInto":[makeQuery(id+"F12.opFillet","BLEND_FACE",FACE,{"disambiguationData":[OSD([subQ0,sQuery(id+"F8.wireOp",EDGE,"E20")])]})]});}
            fillet(context, id + "F16", {"entities" : qUnion([Q0, Q1, Q2, Q3, Q4, Q5, Q6, Q7, Q8, Q9, Q10, Q11, Q12, Q13, Q14, Q15, Q16, Q17, Q18, Q19, Q20, Q21, Q22, Q23, Q24, Q25, Q26, Q27]), "radius" : 2 * mm, "tangentPropagation" : true, "allowEdgeOverflow" : false});
        }
        {
            var Q0;
            Q0=qCreatedBy(makeId("Right.planeOp"),FACE);
            var sketch = newSketch(context, id + "F17", { "sketchPlane" : qUnion([Q0])});
            skPoint(sketch, "E35", {"position": v(-20, 81.08) * mm});
            skPoint(sketch, "E36", {"position": v(-20, 38.66) * mm});
            skLineSegment(sketch, "E37", {"start": v(-20, 81.08) * mm, "end": v(-20, 38.66) * mm, "construction": true});
            skPoint(sketch, "E38", {"position": v(-20, 59.87) * mm});
            skPoint(sketch, "E39", {"position": v(-15.92, 59.87) * mm});
            skPoint(sketch, "E40", {"position": v(-15.92, 81.08) * mm});
            skPoint(sketch, "E41", {"position": v(-15.92, 38.66) * mm});
            skLineSegment(sketch, "E42", {"start": v(-15.92, 81.08) * mm, "end": v(-15.92, 59.87) * mm, "construction": true});
            skLineSegment(sketch, "E43", {"start": v(-15.92, 38.66) * mm, "end": v(-15.92, 59.87) * mm, "construction": true});
            skPoint(sketch, "E44", {"position": v(-15.92, 70.48) * mm});
            skPoint(sketch, "E45", {"position": v(-15.92, 49.26) * mm});
            skPoint(sketch, "E46", {"position": v(-20, 49.26) * mm});
            skPoint(sketch, "E47", {"position": v(-20, 70.48) * mm});
            skLineSegment(sketch, "E48", {"start": v(-20, 70.48) * mm, "end": v(-15.92, 70.48) * mm, "construction": true});
            skLineSegment(sketch, "E49", {"start": v(-20, 49.26) * mm, "end": v(-15.92, 49.26) * mm, "construction": true});
            skPoint(sketch, "E50", {"position": v(-17.96, 70.48) * mm});
            skPoint(sketch, "E51", {"position": v(-17.96, 49.26) * mm});
            skCircle(sketch, "E52", {"center": v(-17.96, 70.48) * mm, "radius": 2 * mm});
            skCircle(sketch, "E53", {"center": v(-17.96, 49.26) * mm, "radius": 2 * mm});
            skPoint(sketch, "E54", {"position": v(-14.92, 70.48) * mm});
            skPoint(sketch, "E55", {"position": v(-14.92, 49.26) * mm});
            skCircle(sketch, "E56.cCircle", {"center": v(-17.96, 70.48) * mm, "radius": 3.04 * mm, "construction": true});
            skLineSegment(sketch, "E56.0", {"start": v(-14.92, 72.23) * mm, "end": v(-14.92, 68.72) * mm});
            skLineSegment(sketch, "E56.1", {"start": v(-14.92, 68.72) * mm, "end": v(-17.96, 66.97) * mm});
            skLineSegment(sketch, "E56.2", {"start": v(-17.96, 66.97) * mm, "end": v(-21, 68.72) * mm});
            skLineSegment(sketch, "E56.3", {"start": v(-21, 68.72) * mm, "end": v(-21, 72.23) * mm});
            skLineSegment(sketch, "E56.4", {"start": v(-21, 72.23) * mm, "end": v(-17.96, 73.98) * mm});
            skLineSegment(sketch, "E56.5", {"start": v(-17.96, 73.98) * mm, "end": v(-14.92, 72.23) * mm});
            skPoint(sketch, "E57.0.midPoint", {"position": v(-15.3, 49.26) * mm});
            skCircle(sketch, "E58.cCircle", {"center": v(-17.96, 49.26) * mm, "radius": 3.04 * mm, "construction": true});
            skLineSegment(sketch, "E58.0", {"start": v(-14.92, 51.02) * mm, "end": v(-14.92, 47.5) * mm});
            skLineSegment(sketch, "E58.1", {"start": v(-14.92, 47.5) * mm, "end": v(-17.96, 45.76) * mm});
            skLineSegment(sketch, "E58.2", {"start": v(-17.96, 45.76) * mm, "end": v(-21, 47.5) * mm});
            skLineSegment(sketch, "E58.3", {"start": v(-21, 47.5) * mm, "end": v(-21, 51.02) * mm});
            skLineSegment(sketch, "E58.4", {"start": v(-21, 51.02) * mm, "end": v(-17.96, 52.77) * mm});
            skLineSegment(sketch, "E58.5", {"start": v(-17.96, 52.77) * mm, "end": v(-14.92, 51.02) * mm});
            skSolve(sketch);
        }
        {
            var Q0;
            Q0=makeQuery(id+"F17.imprint","IMPRINT",FACE,{"disambiguationData":[TD([[makeQuery(id+"F17.imprint","IMPRINT",EDGE,{"derivedFrom":sQuery(id+"F17.wireOp",EDGE,"E52")}),1.0]])]});
            var Q1;
            Q1=makeQuery(id+"F17.imprint","IMPRINT",FACE,{"disambiguationData":[TD([[makeQuery(id+"F17.imprint","IMPRINT",EDGE,{"derivedFrom":sQuery(id+"F17.wireOp",EDGE,"E53")}),1.0]])]});
            var Q2;
            Q2=sQuery(id+"F17.wireOp",EDGE,"E52");
            var Q3;
            Q3=sQuery(id+"F17.wireOp",EDGE,"E53");
            extrude(context, id + "F18", {"entities" : qUnion([Q0, Q1]), "operationType" : NewBodyOperationType.REMOVE, "surfaceEntities" : qUnion([Q2, Q3]), "depth" : 25 * mm, "symmetric" : true});
        }
        {
            var Q0;
            {var subQ1=sQuery(id+"F8.wireOp",EDGE,"E22");Q0=makeQuery(id+"F18.boolean.opBoolean","INTERSECT",EDGE,{"derivedFrom":[makeQuery(id+"F10.boolean.opBoolean","SPLIT",FACE,{"disambiguationData":[TD([makeQuery(id+"F2.opExtrude","SWEPT_FACE",FACE,{"disambiguationData":[OSD([sQuery(id+"F0.wireOp",EDGE,"E3")])]})])],"derivedFrom":makeQuery(id+"F10.opExtrude","SWEPT_FACE",FACE,{"disambiguationData":[OSD([subQ1])]})}),makeQuery(id+"F18.opExtrude","SWEPT_FACE",FACE,{"disambiguationData":[OSD([sQuery(id+"F17.wireOp",EDGE,"E52")])]})]});}
            var Q1;
            {var subQ1=sQuery(id+"F8.wireOp",EDGE,"E22");Q1=makeQuery(id+"F18.boolean.opBoolean","INTERSECT",EDGE,{"derivedFrom":[makeQuery(id+"F10.boolean.opBoolean","SPLIT",FACE,{"disambiguationData":[TD([makeQuery(id+"F2.opExtrude","SWEPT_FACE",FACE,{"disambiguationData":[OSD([sQuery(id+"F0.wireOp",EDGE,"E3")])]})])],"derivedFrom":makeQuery(id+"F10.opExtrude","SWEPT_FACE",FACE,{"disambiguationData":[OSD([subQ1])]})}),makeQuery(id+"F18.opExtrude","SWEPT_FACE",FACE,{"disambiguationData":[OSD([sQuery(id+"F17.wireOp",EDGE,"E53")])]})]});}
            chamfer(context, id + "F19", {"entities" : qUnion([Q0, Q1]), "width" : 1 * mm, "tangentPropagation" : true});
        }
        {
            var Q0;
            Q0=makeQuery(id+"F17.imprint","IMPRINT",FACE,{"disambiguationData":[TD([[makeQuery(id+"F17.imprint","IMPRINT",EDGE,{"derivedFrom":sQuery(id+"F17.wireOp",EDGE,"E52")}),-1.0]])]});
            var Q1;
            Q1=makeQuery(id+"F17.imprint","IMPRINT",FACE,{"disambiguationData":[TD([[makeQuery(id+"F17.imprint","IMPRINT",EDGE,{"derivedFrom":sQuery(id+"F17.wireOp",EDGE,"E53")}),-1.0]])]});
            extrude(context, id + "F20", {"entities" : qUnion([Q0, Q1]), "operationType" : NewBodyOperationType.REMOVE, "depth" : 25 * mm, "hasSecondDirection" : true, "secondDirectionOppositeDirection" : false, "secondDirectionDepth" : 5.5 * mm});
        }
    });
